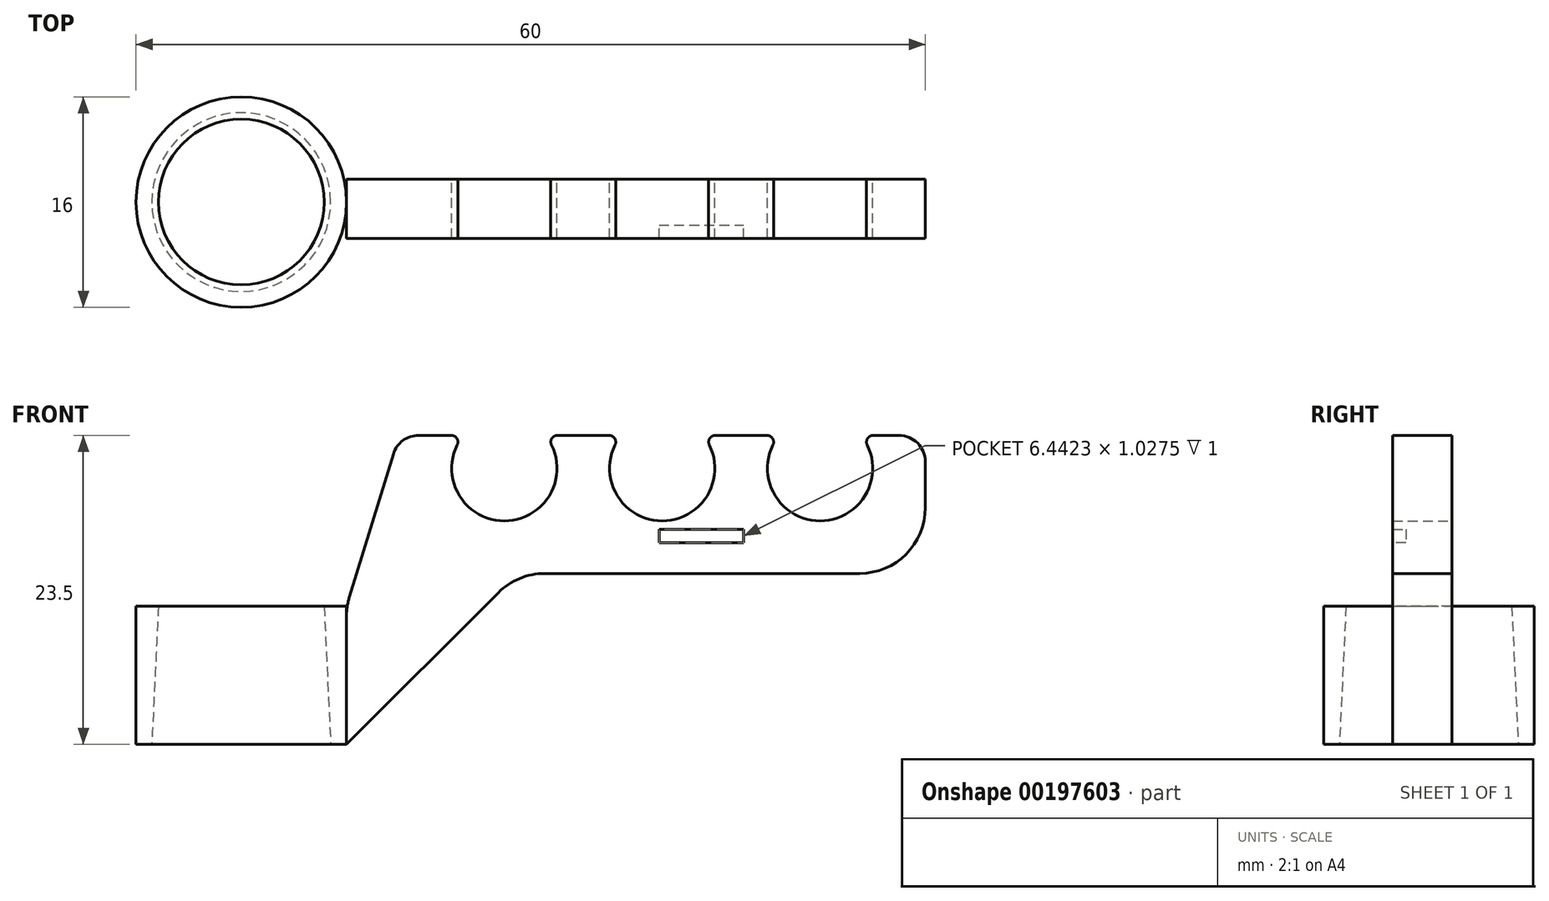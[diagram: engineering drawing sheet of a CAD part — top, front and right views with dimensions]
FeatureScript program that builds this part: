
annotation { "Feature Type Name" : "Feature", "Feature Type Description" : "" }
export const myFeature = defineFeature(function(context is Context, id is Id, definition is map)
    precondition{}
    {
        {
            var Q0;
            Q0=qCreatedBy(makeId("Top.planeOp"),FACE);
            var sketch = newSketch(context, id + "F0", { "sketchPlane" : qUnion([Q0])});
            skCircle(sketch, "E0", {"center": v(0, 0) * mm, "radius": 6.3 * mm});
            skCircle(sketch, "E1", {"center": v(0, 0) * mm, "radius": 8 * mm});
            skCircle(sketch, "E2", {"center": v(0, 0) * mm, "radius": 6.8 * mm});
            skSolve(sketch);
        }
        {
            var Q0;
            Q0=qCreatedBy(makeId("Front.planeOp"),FACE);
            var sketch = newSketch(context, id + "F1", { "sketchPlane" : qUnion([Q0])});
            skLineSegment(sketch, "E3.0", {"start": v(-6.8, 0) * mm, "end": v(6.8, 0) * mm});
            skLineSegment(sketch, "E4.0", {"start": v(-6.3, 0) * mm, "end": v(6.3, 0) * mm});
            skLineSegment(sketch, "E5.0", {"start": v(-8, 0) * mm, "end": v(-5.58, 0) * mm});
            skLineSegment(sketch, "E6", {"start": v(0, 0) * mm, "end": v(0, 10.5) * mm});
            skLineSegment(sketch, "E7.top", {"start": v(-8, 10.5) * mm, "end": v(-6.3, 10.5) * mm});
            skLineSegment(sketch, "E7.left", {"start": v(-8, 0) * mm, "end": v(-8, 10.5) * mm});
            skLineSegment(sketch, "E8", {"start": v(-6.3, 10.5) * mm, "end": v(-6.8, 0) * mm});
            skLineSegment(sketch, "E9.trimOffspring", {"start": v(0, 0) * mm, "end": v(8, 0) * mm});
            skSolve(sketch);
        }
        {
            var Q0;
            Q0=makeQuery(id+"F1.imprint","IMPRINT",FACE,{"disambiguationData":[TD([[makeQuery(id+"F1.imprint","IMPRINT",EDGE,{"derivedFrom":sQuery(id+"F1.wireOp",EDGE,"E7.top")}),-1.0]])]});
            var Q1;
            Q1=sQuery(id+"F1.wireOp",EDGE,"E6");
            revolve(context, id + "F2", {"entities" : qUnion([Q0]), "axis" : qUnion([Q1]), "revolveType" : RevolveType.FULL});
        }
        {
            var Q0;
            Q0=qCreatedBy(makeId("Front.planeOp"),FACE);
            var sketch = newSketch(context, id + "F3", { "sketchPlane" : qUnion([Q0])});
            skLineSegment(sketch, "E10", {"start": v(8, 10.5) * mm, "end": v(8, 0) * mm});
            skLineSegment(sketch, "E11.0", {"start": v(8, 10.5) * mm, "end": v(-8, 10.5) * mm});
            skLineSegment(sketch, "E12.0", {"start": v(-8, 0) * mm, "end": v(8, 0) * mm});
            skLineSegment(sketch, "E13", {"start": v(0, 13) * mm, "end": v(41.13, 13) * mm, "construction": true});
            skLineSegment(sketch, "E14", {"start": v(0, 21) * mm, "end": v(40.48, 21) * mm, "construction": true});
            skLineSegment(sketch, "E15", {"start": v(20, 25.73) * mm, "end": v(20, 4.34) * mm, "construction": true});
            skCircle(sketch, "E16", {"center": v(20, 21) * mm, "radius": 4 * mm});
            skCircle(sketch, "E17.1.0.0", {"center": v(32, 21) * mm, "radius": 4 * mm});
            skCircle(sketch, "E17.2.0.0", {"center": v(44, 21) * mm, "radius": 4 * mm});
            skLineSegment(sketch, "E17.direction1", {"start": v(20, 21) * mm, "end": v(32, 21) * mm, "construction": true});
            skLineSegment(sketch, "E18", {"start": v(12, 25.64) * mm, "end": v(12, 16.43) * mm, "construction": true});
            skLineSegment(sketch, "E19", {"start": v(12, 23.5) * mm, "end": v(68.02, 23.5) * mm});
            skLineSegment(sketch, "E20", {"start": v(52, 26.61) * mm, "end": v(52, 15.45) * mm, "construction": true});
            skLineSegment(sketch, "E21", {"start": v(12, 23.5) * mm, "end": v(8, 10.5) * mm});
            skLineSegment(sketch, "E22", {"start": v(22.25, 13) * mm, "end": v(41.13, 13) * mm});
            skLineSegment(sketch, "E23", {"start": v(52, 13) * mm, "end": v(52, 23.5) * mm});
            skLineSegment(sketch, "E24", {"start": v(8, 0) * mm, "end": v(21, 13) * mm});
            skPoint(sketch, "E25.orphan", {"position": v(22.25, 14.25) * mm});
            skLineSegment(sketch, "E26", {"start": v(21, 13) * mm, "end": v(22.25, 13) * mm});
            skLineSegment(sketch, "E27", {"start": v(41.13, 13) * mm, "end": v(52, 13) * mm});
            skLineSegment(sketch, "E28.bottom", {"start": v(8, 10.5) * mm, "end": v(7.8, 10.5) * mm});
            skLineSegment(sketch, "E28.top", {"start": v(8, 0) * mm, "end": v(7.8, 0) * mm});
            skLineSegment(sketch, "E28.right", {"start": v(7.8, 10.5) * mm, "end": v(7.8, 0) * mm});
            skSolve(sketch);
        }
        {
            var Q0;
            {var subQ0=sQuery(id+"F3.wireOp",EDGE,"E21");Q0=makeQuery(id+"F3.imprint","IMPRINT",FACE,{"disambiguationData":[TD([[makeQuery(id+"F3.imprint","IMPRINT",EDGE,{"derivedFrom":subQ0}),1.0]])]});}
            var Q1;
            Q1=makeQuery(id+"F3.imprint","IMPRINT",FACE,{"disambiguationData":[TD([[makeQuery(id+"F3.imprint","IMPRINT",EDGE,{"derivedFrom":sQuery(id+"F3.wireOp",EDGE,"E28.bottom")}),1.0]])]});
            extrude(context, id + "F4", {"entities" : qUnion([Q0, Q1]), "operationType" : NewBodyOperationType.ADD, "endBound" : BoundingType.SYMMETRIC, "depth" : 3.5 * mm});
        }
        {
            var Q0;
            Q0=makeQuery(id+"F4.boolean.opBoolean","INTERSECT",EDGE,{"derivedFrom":[makeQuery(id+"F2.opRevolve","SWEPT_FACE",FACE,{"disambiguationData":[OSD([sQuery(id+"F1.wireOp",EDGE,"E7.left")])]}),makeQuery(id+"F4.opExtrude","CAP_FACE",FACE,{"disambiguationData":[OSD([sQuery(id+"F3.wireOp",EDGE,"E16"),sQuery(id+"F3.wireOp",EDGE,"E17.1.0.0"),sQuery(id+"F3.wireOp",EDGE,"E17.2.0.0"),sQuery(id+"F3.wireOp",EDGE,"E17.3.0.0"),sQuery(id+"F3.wireOp",EDGE,"E19"),sQuery(id+"F3.wireOp",EDGE,"E21"),sQuery(id+"F3.wireOp",EDGE,"E22"),sQuery(id+"F3.wireOp",EDGE,"E23"),sQuery(id+"F3.wireOp",EDGE,"E24"),sQuery(id+"F3.wireOp",EDGE,"E26"),sQuery(id+"F3.wireOp",EDGE,"E27"),sQuery(id+"F3.wireOp",EDGE,"E28.bottom"),sQuery(id+"F3.wireOp",EDGE,"E28.top"),sQuery(id+"F3.wireOp",EDGE,"E28.right")])],"isStart":true})]});
            var Q1;
            Q1=makeQuery(id+"F4.boolean.opBoolean","INTERSECT",EDGE,{"derivedFrom":[makeQuery(id+"F2.opRevolve","SWEPT_FACE",FACE,{"disambiguationData":[OSD([sQuery(id+"F1.wireOp",EDGE,"E7.left")])]}),makeQuery(id+"F4.opExtrude","CAP_FACE",FACE,{"disambiguationData":[OSD([sQuery(id+"F3.wireOp",EDGE,"E16"),sQuery(id+"F3.wireOp",EDGE,"E17.1.0.0"),sQuery(id+"F3.wireOp",EDGE,"E17.2.0.0"),sQuery(id+"F3.wireOp",EDGE,"E17.3.0.0"),sQuery(id+"F3.wireOp",EDGE,"E19"),sQuery(id+"F3.wireOp",EDGE,"E21"),sQuery(id+"F3.wireOp",EDGE,"E22"),sQuery(id+"F3.wireOp",EDGE,"E23"),sQuery(id+"F3.wireOp",EDGE,"E24"),sQuery(id+"F3.wireOp",EDGE,"E26"),sQuery(id+"F3.wireOp",EDGE,"E27"),sQuery(id+"F3.wireOp",EDGE,"E28.bottom"),sQuery(id+"F3.wireOp",EDGE,"E28.top"),sQuery(id+"F3.wireOp",EDGE,"E28.right")])],"isStart":false})]});
            var Q2;
            Q2=makeQuery(id+"F4.opExtrude","SWEPT_EDGE",EDGE,{"disambiguationData":[OSD([sQuery(id+"F3.wireOp",EDGE,"E24"),sQuery(id+"F3.wireOp",EDGE,"E26")])]});
            var Q3;
            Q3=makeQuery(id+"F4.opExtrude","SWEPT_EDGE",EDGE,{"disambiguationData":[OSD([sQuery(id+"F3.wireOp",EDGE,"E23"),sQuery(id+"F3.wireOp",EDGE,"E27")])]});
            fillet(context, id + "F5", {"entities" : qUnion([Q0, Q1, Q2, Q3]), "radius" : 5 * mm, "tangentPropagation" : true, "allowEdgeOverflow" : false});
        }
        {
            var Q0;
            Q0=makeQuery(id+"F4.opExtrude","SWEPT_EDGE",EDGE,{"disambiguationData":[OSD([sQuery(id+"F3.wireOp",EDGE,"E19"),sQuery(id+"F3.wireOp",EDGE,"E21")])]});
            var Q1;
            Q1=makeQuery(id+"F4.opExtrude","SWEPT_EDGE",EDGE,{"disambiguationData":[OSD([sQuery(id+"F3.wireOp",EDGE,"E19"),sQuery(id+"F3.wireOp",EDGE,"E23")])]});
            fillet(context, id + "F6", {"entities" : qUnion([Q0, Q1]), "radius" : 2 * mm, "tangentPropagation" : true, "allowEdgeOverflow" : false});
        }
        {
            var Q0;
            {var subQ0=sQuery(id+"F3.wireOp",EDGE,"E19");var subQ1=sQuery(id+"F3.wireOp",EDGE,"E16");Q0=makeQuery(id+"F4.opExtrude","SWEPT_EDGE",EDGE,{"disambiguationData":[OSD([subQ1,subQ0]),TDD([makeQuery(id+"F3.imprint","INTERSECT",VERTEX,{"disambiguationData":[OD(1.0)],"derivedFrom":[subQ1,subQ0]})])]});}
            var Q1;
            {var subQ0=sQuery(id+"F3.wireOp",EDGE,"E19");var subQ1=sQuery(id+"F3.wireOp",EDGE,"E16");Q1=makeQuery(id+"F4.opExtrude","SWEPT_EDGE",EDGE,{"disambiguationData":[OSD([subQ1,subQ0]),TDD([makeQuery(id+"F3.imprint","INTERSECT",VERTEX,{"disambiguationData":[OD(0.0)],"derivedFrom":[subQ1,subQ0]})])]});}
            var Q2;
            {var subQ0=sQuery(id+"F3.wireOp",EDGE,"E19");var subQ1=sQuery(id+"F3.wireOp",EDGE,"E17.1.0.0");Q2=makeQuery(id+"F4.opExtrude","SWEPT_EDGE",EDGE,{"disambiguationData":[OSD([subQ1,subQ0]),TDD([makeQuery(id+"F3.imprint","INTERSECT",VERTEX,{"disambiguationData":[OD(0.0)],"derivedFrom":[subQ1,subQ0]})])]});}
            var Q3;
            {var subQ0=sQuery(id+"F3.wireOp",EDGE,"E19");var subQ1=sQuery(id+"F3.wireOp",EDGE,"E17.2.0.0");Q3=makeQuery(id+"F4.opExtrude","SWEPT_EDGE",EDGE,{"disambiguationData":[OSD([subQ1,subQ0]),TDD([makeQuery(id+"F3.imprint","INTERSECT",VERTEX,{"disambiguationData":[OD(0.0)],"derivedFrom":[subQ1,subQ0]})])]});}
            var Q4;
            {var subQ0=sQuery(id+"F3.wireOp",EDGE,"E19");var subQ1=sQuery(id+"F3.wireOp",EDGE,"E17.3.0.0");Q4=makeQuery(id+"F4.opExtrude","SWEPT_EDGE",EDGE,{"disambiguationData":[OSD([subQ1,subQ0]),TDD([makeQuery(id+"F3.imprint","INTERSECT",VERTEX,{"disambiguationData":[OD(0.0)],"derivedFrom":[subQ1,subQ0]})])]});}
            var Q5;
            {var subQ0=sQuery(id+"F3.wireOp",EDGE,"E19");var subQ1=sQuery(id+"F3.wireOp",EDGE,"E17.1.0.0");Q5=makeQuery(id+"F4.opExtrude","SWEPT_EDGE",EDGE,{"disambiguationData":[OSD([subQ1,subQ0]),TDD([makeQuery(id+"F3.imprint","INTERSECT",VERTEX,{"disambiguationData":[OD(1.0)],"derivedFrom":[subQ1,subQ0]})])]});}
            var Q6;
            {var subQ0=sQuery(id+"F3.wireOp",EDGE,"E19");var subQ1=sQuery(id+"F3.wireOp",EDGE,"E17.2.0.0");Q6=makeQuery(id+"F4.opExtrude","SWEPT_EDGE",EDGE,{"disambiguationData":[OSD([subQ1,subQ0]),TDD([makeQuery(id+"F3.imprint","INTERSECT",VERTEX,{"disambiguationData":[OD(1.0)],"derivedFrom":[subQ1,subQ0]})])]});}
            var Q7;
            {var subQ0=sQuery(id+"F3.wireOp",EDGE,"E19");var subQ1=sQuery(id+"F3.wireOp",EDGE,"E17.3.0.0");Q7=makeQuery(id+"F4.opExtrude","SWEPT_EDGE",EDGE,{"disambiguationData":[OSD([subQ1,subQ0]),TDD([makeQuery(id+"F3.imprint","INTERSECT",VERTEX,{"disambiguationData":[OD(1.0)],"derivedFrom":[subQ1,subQ0]})])]});}
            fillet(context, id + "F7", {"entities" : qUnion([Q0, Q1, Q2, Q3, Q4, Q5, Q6, Q7]), "radius" : .5 * mm, "tangentPropagation" : true, "allowEdgeOverflow" : false});
        }
        {
            var Q0;
            Q0=makeQuery(id+"F4.opExtrude","CAP_FACE",FACE,{"disambiguationData":[OSD([sQuery(id+"F3.wireOp",EDGE,"E16"),sQuery(id+"F3.wireOp",EDGE,"E17.1.0.0"),sQuery(id+"F3.wireOp",EDGE,"E17.2.0.0"),sQuery(id+"F3.wireOp",EDGE,"E17.3.0.0"),sQuery(id+"F3.wireOp",EDGE,"E19"),sQuery(id+"F3.wireOp",EDGE,"E21"),sQuery(id+"F3.wireOp",EDGE,"E22"),sQuery(id+"F3.wireOp",EDGE,"E23"),sQuery(id+"F3.wireOp",EDGE,"E24"),sQuery(id+"F3.wireOp",EDGE,"E26"),sQuery(id+"F3.wireOp",EDGE,"E27"),sQuery(id+"F3.wireOp",EDGE,"E28.bottom"),sQuery(id+"F3.wireOp",EDGE,"E28.top"),sQuery(id+"F3.wireOp",EDGE,"E28.right")])],"isStart":false});
            var sketch = newSketch(context, id + "F8", { "sketchPlane" : qUnion([Q0])});
            skFitSpline(sketch, "E29", {"points": [v(35.71, 16.35) * mm, v(35.78, 16.55) * mm, v(35.85, 16.65) * mm, v(35.98, 16.75) * mm, v(36.12, 16.8) * mm, v(36.24, 16.8) * mm, v(42.55, 16.82) * mm, v(42.65, 16.78) * mm, v(42.7, 16.65) * mm, v(42.65, 16.52) * mm, v(42.55, 16.36) * mm, v(42.42, 16.32) * mm, v(42.3, 16.26) * mm, v(42.08, 15.9) * mm, v(41.89, 15.83) * mm, v(41.78, 15.76) * mm, v(41.62, 15.48) * mm, v(41.45, 15.38) * mm, v(38.77, 14.57) * mm, v(38.7, 14.56) * mm, v(38.62, 14.38) * mm, v(38.56, 14.27) * mm, v(38.18, 14.06) * mm, v(38.06, 14.02) * mm, v(35.9, 13.44) * mm, v(35.75, 13.44) * mm, v(35.65, 13.48) * mm, v(35.59, 13.53) * mm, v(35, 14.06) * mm, v(34.97, 14.05) * mm, v(34.9, 14.03) * mm, v(34.85, 14) * mm, v(34.31, 13.47) * mm, v(34.24, 13.44) * mm, v(34.16, 13.44) * mm, v(31.77, 14.07) * mm, v(31.41, 14.28) * mm, v(31.3, 14.48) * mm, v(31.22, 14.57) * mm, v(31.12, 14.6) * mm, v(28.44, 15.4) * mm, v(28.33, 15.52) * mm, v(28.2, 15.88) * mm, v(28.14, 15.83) * mm, v(28.02, 15.85) * mm, v(27.94, 15.87) * mm, v(27.88, 15.92) * mm, v(27.69, 16.27) * mm, v(27.65, 16.3) * mm, v(27.51, 16.3) * mm, v(27.46, 16.32) * mm, v(27.28, 16.62) * mm, v(27.28, 16.7) * mm, v(27.33, 16.77) * mm, v(27.4, 16.8) * mm, v(27.46, 16.8) * mm, v(33.8, 16.81) * mm, v(33.85, 16.81) * mm, v(33.97, 16.77) * mm, v(34.17, 16.6) * mm, v(34.2, 16.5) * mm, v(34.25, 16.4) * mm, v(34.26, 16.34) * mm, v(34.33, 16.34) * mm, v(35.58, 16.34) * mm, v(35.71, 16.35) * mm]});
            skFitSpline(sketch, "E30", {"points": [v(30.68, 16.8) * mm, v(30.83, 16.69) * mm, v(30.9, 16.62) * mm, v(30.99, 16.5) * mm, v(31.06, 16.33) * mm, v(31.28, 16.02) * mm, v(31.53, 15.67) * mm, v(31.6, 15.6) * mm, v(32.13, 15.09) * mm, v(32.73, 14.67) * mm, v(33.36, 14.37) * mm, v(33.87, 14.2) * mm, v(34.55, 14.1) * mm, v(35, 14.06) * mm, v(35.61, 14.1) * mm, v(36.24, 14.24) * mm, v(36.81, 14.44) * mm, v(37.3, 14.7) * mm, v(37.8, 15.05) * mm, v(38.1, 15.33) * mm, v(38.48, 15.75) * mm, v(38.72, 16.05) * mm, v(38.93, 16.39) * mm, v(39.08, 16.63) * mm, v(39.22, 16.76) * mm, v(39.4, 16.82) * mm, v(39.46, 16.82) * mm], "startDerivative": vector(6.61, -4.14) * mm, "endDerivative": vector(2.94, -0.27) * mm});
            skLineSegment(sketch, "E31.bottom", {"start": v(31.76, 16.35) * mm, "end": v(38.2, 16.35) * mm});
            skLineSegment(sketch, "E31.top", {"start": v(31.76, 15.33) * mm, "end": v(38.2, 15.33) * mm});
            skLineSegment(sketch, "E31.left", {"start": v(31.76, 16.35) * mm, "end": v(31.76, 15.33) * mm});
            skLineSegment(sketch, "E31.right", {"start": v(38.2, 16.35) * mm, "end": v(38.2, 15.33) * mm});
            skLineSegment(sketch, "E32", {"start": v(27.69, 16.27) * mm, "end": v(31.76, 16.35) * mm});
            skLineSegment(sketch, "E33", {"start": v(31.76, 16.1) * mm, "end": v(28.2, 15.88) * mm});
            skLineSegment(sketch, "E34", {"start": v(31.76, 15.88) * mm, "end": v(28.44, 15.4) * mm});
            skLineSegment(sketch, "E35", {"start": v(31.76, 15.67) * mm, "end": v(29.25, 15.15) * mm});
            skLineSegment(sketch, "E36", {"start": v(31.76, 15.33) * mm, "end": v(30.28, 14.84) * mm});
            skLineSegment(sketch, "E37", {"start": v(32.82, 15.33) * mm, "end": v(31.22, 14.57) * mm});
            skLineSegment(sketch, "E38", {"start": v(33.59, 15.33) * mm, "end": v(31.77, 14.07) * mm});
            skLineSegment(sketch, "E39", {"start": v(34.05, 15.33) * mm, "end": v(32.59, 13.83) * mm});
            skLineSegment(sketch, "E40", {"start": v(34.4, 15.33) * mm, "end": v(33.39, 13.61) * mm});
            skLineSegment(sketch, "E41", {"start": v(34.73, 15.33) * mm, "end": v(34.16, 13.44) * mm});
            skLineSegment(sketch, "E42", {"start": v(34.98, 15.33) * mm, "end": v(34.97, 14.05) * mm});
            skLineSegment(sketch, "E43", {"start": v(35.26, 15.33) * mm, "end": v(35.81, 13.43) * mm});
            skLineSegment(sketch, "E44", {"start": v(35.61, 15.33) * mm, "end": v(36.58, 13.6) * mm});
            skLineSegment(sketch, "E45", {"start": v(35.96, 15.33) * mm, "end": v(37.37, 13.83) * mm});
            skLineSegment(sketch, "E46", {"start": v(36.38, 15.33) * mm, "end": v(38.18, 14.06) * mm});
            skLineSegment(sketch, "E47", {"start": v(37.14, 15.33) * mm, "end": v(38.77, 14.57) * mm});
            skLineSegment(sketch, "E48", {"start": v(38.2, 15.33) * mm, "end": v(39.77, 14.85) * mm});
            skLineSegment(sketch, "E49", {"start": v(38.2, 15.65) * mm, "end": v(40.68, 15.13) * mm});
            skLineSegment(sketch, "E50", {"start": v(38.2, 15.87) * mm, "end": v(41.57, 15.43) * mm});
            skLineSegment(sketch, "E51", {"start": v(38.2, 16.1) * mm, "end": v(42.02, 15.86) * mm});
            skLineSegment(sketch, "E52", {"start": v(38.2, 16.3) * mm, "end": v(42.35, 16.3) * mm});
            skSolve(sketch);
        }
        {
            var Q0;
            {var subQ0=sQuery(id+"F8.wireOp",EDGE,"E36");Q0=makeQuery(id+"F8.imprint","IMPRINT",FACE,{"disambiguationData":[TD([[makeQuery(id+"F8.imprint","IMPRINT",EDGE,{"derivedFrom":subQ0}),-1.0]])]});}
            var Q1;
            {var subQ0=sQuery(id+"F8.wireOp",EDGE,"E46");var subQ1=sQuery(id+"F8.wireOp",EDGE,"E29");var subQ2=makeQuery(id+"F8.imprint","INTERSECT",VERTEX,{"derivedFrom":[subQ1,subQ0]});Q1=makeQuery(id+"F8.imprint","IMPRINT",FACE,{"disambiguationData":[TD([[makeQuery(id+"F8.imprint","IMPRINT",EDGE,{"disambiguationData":[TD([[subQ2,1.0]])],"derivedFrom":subQ1}),-1.0]])]});}
            var Q2;
            {var subQ0=sQuery(id+"F8.wireOp",EDGE,"E38");var subQ1=sQuery(id+"F8.wireOp",EDGE,"E29");var subQ2=makeQuery(id+"F8.imprint","INTERSECT",VERTEX,{"derivedFrom":[subQ1,subQ0]});Q2=makeQuery(id+"F8.imprint","IMPRINT",FACE,{"disambiguationData":[TD([[makeQuery(id+"F8.imprint","IMPRINT",EDGE,{"disambiguationData":[TD([[subQ2,1.0]])],"derivedFrom":subQ1}),-1.0]])]});}
            var Q3;
            {var subQ0=sQuery(id+"F8.wireOp",EDGE,"E44");var subQ1=sQuery(id+"F8.wireOp",EDGE,"E30");var subQ2=makeQuery(id+"F8.imprint","INTERSECT",VERTEX,{"derivedFrom":[subQ1,subQ0]});Q3=makeQuery(id+"F8.imprint","IMPRINT",FACE,{"disambiguationData":[TD([[makeQuery(id+"F8.imprint","IMPRINT",EDGE,{"disambiguationData":[TD([[subQ2,-1.0]])],"derivedFrom":subQ1}),1.0]])]});}
            var Q4;
            {var subQ0=sQuery(id+"F8.wireOp",EDGE,"E39");var subQ1=sQuery(id+"F8.wireOp",EDGE,"E29");var subQ2=makeQuery(id+"F8.imprint","INTERSECT",VERTEX,{"derivedFrom":[subQ1,subQ0]});Q4=makeQuery(id+"F8.imprint","IMPRINT",FACE,{"disambiguationData":[TD([[makeQuery(id+"F8.imprint","IMPRINT",EDGE,{"disambiguationData":[TD([[subQ2,1.0]])],"derivedFrom":subQ1}),-1.0]])]});}
            var Q5;
            {var subQ0=sQuery(id+"F8.wireOp",EDGE,"E43");var subQ1=sQuery(id+"F8.wireOp",EDGE,"E30");var subQ2=makeQuery(id+"F8.imprint","INTERSECT",VERTEX,{"derivedFrom":[subQ1,subQ0]});Q5=makeQuery(id+"F8.imprint","IMPRINT",FACE,{"disambiguationData":[TD([[makeQuery(id+"F8.imprint","IMPRINT",EDGE,{"disambiguationData":[TD([[subQ2,-1.0]])],"derivedFrom":subQ1}),1.0]])]});}
            var Q6;
            {var subQ0=sQuery(id+"F8.wireOp",EDGE,"E30");var subQ1=sQuery(id+"F8.wireOp",EDGE,"E29");var subQ2=makeQuery(id+"F8.imprint","INTERSECT",VERTEX,{"disambiguationData":[OD(0.0)],"derivedFrom":[subQ1,subQ0]});Q6=makeQuery(id+"F8.imprint","IMPRINT",FACE,{"disambiguationData":[TD([[makeQuery(id+"F8.imprint","IMPRINT",EDGE,{"disambiguationData":[TD([[subQ2,-1.0]])],"derivedFrom":subQ1}),-1.0]])]});}
            var Q7;
            {var subQ0=sQuery(id+"F8.wireOp",EDGE,"E41");var subQ1=sQuery(id+"F8.wireOp",EDGE,"E30");var subQ2=makeQuery(id+"F8.imprint","INTERSECT",VERTEX,{"derivedFrom":[subQ1,subQ0]});Q7=makeQuery(id+"F8.imprint","IMPRINT",FACE,{"disambiguationData":[TD([[makeQuery(id+"F8.imprint","IMPRINT",EDGE,{"disambiguationData":[TD([[subQ2,-1.0]])],"derivedFrom":subQ1}),1.0]])]});}
            var Q8;
            {var subQ0=sQuery(id+"F8.wireOp",EDGE,"E32");var subQ1=sQuery(id+"F8.wireOp",EDGE,"E30");var subQ2=makeQuery(id+"F8.imprint","INTERSECT",VERTEX,{"derivedFrom":[subQ1,subQ0]});Q8=makeQuery(id+"F8.imprint","IMPRINT",FACE,{"disambiguationData":[TD([[makeQuery(id+"F8.imprint","IMPRINT",EDGE,{"disambiguationData":[TD([[subQ2,-1.0]])],"derivedFrom":subQ1}),1.0]])]});}
            var Q9;
            {var subQ0=sQuery(id+"F8.wireOp",EDGE,"E48");Q9=makeQuery(id+"F8.imprint","IMPRINT",FACE,{"disambiguationData":[TD([[makeQuery(id+"F8.imprint","IMPRINT",EDGE,{"derivedFrom":subQ0}),-1.0]])]});}
            var Q10;
            {var subQ0=sQuery(id+"F8.wireOp",EDGE,"E32");var subQ1=sQuery(id+"F8.wireOp",EDGE,"E29");var subQ2=makeQuery(id+"F8.imprint","INTERSECT",VERTEX,{"derivedFrom":[subQ1,subQ0]});Q10=makeQuery(id+"F8.imprint","IMPRINT",FACE,{"disambiguationData":[TD([[makeQuery(id+"F8.imprint","IMPRINT",EDGE,{"disambiguationData":[TD([[subQ2,1.0]])],"derivedFrom":subQ1}),-1.0]])]});}
            var Q11;
            {var subQ0=sQuery(id+"F8.wireOp",EDGE,"E40");var subQ1=sQuery(id+"F8.wireOp",EDGE,"E30");var subQ2=makeQuery(id+"F8.imprint","INTERSECT",VERTEX,{"derivedFrom":[subQ1,subQ0]});Q11=makeQuery(id+"F8.imprint","IMPRINT",FACE,{"disambiguationData":[TD([[makeQuery(id+"F8.imprint","IMPRINT",EDGE,{"disambiguationData":[TD([[subQ2,-1.0]])],"derivedFrom":subQ1}),1.0]])]});}
            var Q12;
            {var subQ3=sQuery(id+"F8.wireOp",EDGE,"E29");var subQ7=sQuery(id+"F8.wireOp",EDGE,"E30");var subQ8=makeQuery(id+"F8.imprint","INTERSECT",VERTEX,{"disambiguationData":[OD(2.0)],"derivedFrom":[subQ3,subQ7]});Q12=makeQuery(id+"F8.imprint","IMPRINT",FACE,{"disambiguationData":[TD([[makeQuery(id+"F8.imprint","IMPRINT",EDGE,{"disambiguationData":[TD([[subQ8,1.0]])],"derivedFrom":subQ3}),-1.0]])]});}
            var Q13;
            {var subQ0=sQuery(id+"F8.wireOp",EDGE,"E48");Q13=makeQuery(id+"F8.imprint","IMPRINT",FACE,{"disambiguationData":[TD([[makeQuery(id+"F8.imprint","IMPRINT",EDGE,{"derivedFrom":subQ0}),1.0]])]});}
            var Q14;
            {var subQ0=sQuery(id+"F8.wireOp",EDGE,"E33");var subQ1=sQuery(id+"F8.wireOp",EDGE,"E29");var subQ2=makeQuery(id+"F8.imprint","INTERSECT",VERTEX,{"derivedFrom":[subQ1,subQ0]});Q14=makeQuery(id+"F8.imprint","IMPRINT",FACE,{"disambiguationData":[TD([[makeQuery(id+"F8.imprint","IMPRINT",EDGE,{"disambiguationData":[TD([[subQ2,1.0]])],"derivedFrom":subQ1}),-1.0]])]});}
            var Q15;
            {var subQ0=sQuery(id+"F8.wireOp",EDGE,"E39");var subQ1=sQuery(id+"F8.wireOp",EDGE,"E30");var subQ2=makeQuery(id+"F8.imprint","INTERSECT",VERTEX,{"derivedFrom":[subQ1,subQ0]});Q15=makeQuery(id+"F8.imprint","IMPRINT",FACE,{"disambiguationData":[TD([[makeQuery(id+"F8.imprint","IMPRINT",EDGE,{"disambiguationData":[TD([[subQ2,-1.0]])],"derivedFrom":subQ1}),1.0]])]});}
            var Q16;
            {var subQ0=sQuery(id+"F8.wireOp",EDGE,"E34");var subQ1=sQuery(id+"F8.wireOp",EDGE,"E29");var subQ2=makeQuery(id+"F8.imprint","INTERSECT",VERTEX,{"derivedFrom":[subQ1,subQ0]});Q16=makeQuery(id+"F8.imprint","IMPRINT",FACE,{"disambiguationData":[TD([[makeQuery(id+"F8.imprint","IMPRINT",EDGE,{"disambiguationData":[TD([[subQ2,1.0]])],"derivedFrom":subQ1}),-1.0]])]});}
            var Q17;
            {var subQ0=sQuery(id+"F8.wireOp",EDGE,"E46");var subQ1=sQuery(id+"F8.wireOp",EDGE,"E30");var subQ2=makeQuery(id+"F8.imprint","INTERSECT",VERTEX,{"derivedFrom":[subQ1,subQ0]});Q17=makeQuery(id+"F8.imprint","IMPRINT",FACE,{"disambiguationData":[TD([[makeQuery(id+"F8.imprint","IMPRINT",EDGE,{"disambiguationData":[TD([[subQ2,-1.0]])],"derivedFrom":subQ1}),1.0]])]});}
            var Q18;
            {var subQ0=sQuery(id+"F8.wireOp",EDGE,"E38");var subQ1=sQuery(id+"F8.wireOp",EDGE,"E30");var subQ2=makeQuery(id+"F8.imprint","INTERSECT",VERTEX,{"derivedFrom":[subQ1,subQ0]});Q18=makeQuery(id+"F8.imprint","IMPRINT",FACE,{"disambiguationData":[TD([[makeQuery(id+"F8.imprint","IMPRINT",EDGE,{"disambiguationData":[TD([[subQ2,-1.0]])],"derivedFrom":subQ1}),1.0]])]});}
            var Q19;
            {var subQ0=sQuery(id+"F8.wireOp",EDGE,"E36");Q19=makeQuery(id+"F8.imprint","IMPRINT",FACE,{"disambiguationData":[TD([[makeQuery(id+"F8.imprint","IMPRINT",EDGE,{"derivedFrom":subQ0}),1.0]])]});}
            var Q20;
            {var subQ0=sQuery(id+"F8.wireOp",EDGE,"E44");var subQ1=sQuery(id+"F8.wireOp",EDGE,"E29");var subQ2=makeQuery(id+"F8.imprint","INTERSECT",VERTEX,{"derivedFrom":[subQ1,subQ0]});Q20=makeQuery(id+"F8.imprint","IMPRINT",FACE,{"disambiguationData":[TD([[makeQuery(id+"F8.imprint","IMPRINT",EDGE,{"disambiguationData":[TD([[subQ2,1.0]])],"derivedFrom":subQ1}),-1.0]])]});}
            var Q21;
            {var subQ0=sQuery(id+"F8.wireOp",EDGE,"E37");var subQ1=sQuery(id+"F8.wireOp",EDGE,"E30");var subQ2=makeQuery(id+"F8.imprint","INTERSECT",VERTEX,{"derivedFrom":[subQ1,subQ0]});Q21=makeQuery(id+"F8.imprint","IMPRINT",FACE,{"disambiguationData":[TD([[makeQuery(id+"F8.imprint","IMPRINT",EDGE,{"disambiguationData":[TD([[subQ2,-1.0]])],"derivedFrom":subQ1}),1.0]])]});}
            var Q22;
            {var subQ5=sQuery(id+"F8.wireOp",EDGE,"E30");var subQ6=sQuery(id+"F8.wireOp",EDGE,"E29");var subQ9=makeQuery(id+"F8.imprint","INTERSECT",VERTEX,{"disambiguationData":[OD(3.0)],"derivedFrom":[subQ6,subQ5]});Q22=makeQuery(id+"F8.imprint","IMPRINT",FACE,{"disambiguationData":[TD([[makeQuery(id+"F8.imprint","IMPRINT",EDGE,{"disambiguationData":[TD([[subQ9,-1.0]])],"derivedFrom":subQ6}),-1.0]])]});}
            var Q23;
            {var subQ0=sQuery(id+"F8.wireOp",EDGE,"E45");var subQ1=sQuery(id+"F8.wireOp",EDGE,"E29");var subQ2=makeQuery(id+"F8.imprint","INTERSECT",VERTEX,{"derivedFrom":[subQ1,subQ0]});Q23=makeQuery(id+"F8.imprint","IMPRINT",FACE,{"disambiguationData":[TD([[makeQuery(id+"F8.imprint","IMPRINT",EDGE,{"disambiguationData":[TD([[subQ2,1.0]])],"derivedFrom":subQ1}),-1.0]])]});}
            var Q24;
            {var subQ0=sQuery(id+"F8.wireOp",EDGE,"E30");var subQ1=sQuery(id+"F8.wireOp",EDGE,"E29");var subQ2=makeQuery(id+"F8.imprint","INTERSECT",VERTEX,{"disambiguationData":[OD(1.0)],"derivedFrom":[subQ1,subQ0]});Q24=makeQuery(id+"F8.imprint","IMPRINT",FACE,{"disambiguationData":[TD([[makeQuery(id+"F8.imprint","IMPRINT",EDGE,{"disambiguationData":[TD([[subQ2,1.0]])],"derivedFrom":subQ1}),-1.0]])]});}
            var Q25;
            {var subQ0=sQuery(id+"F8.wireOp",EDGE,"E47");var subQ1=sQuery(id+"F8.wireOp",EDGE,"E30");var subQ2=makeQuery(id+"F8.imprint","INTERSECT",VERTEX,{"derivedFrom":[subQ1,subQ0]});Q25=makeQuery(id+"F8.imprint","IMPRINT",FACE,{"disambiguationData":[TD([[makeQuery(id+"F8.imprint","IMPRINT",EDGE,{"disambiguationData":[TD([[subQ2,-1.0]])],"derivedFrom":subQ1}),1.0]])]});}
            var Q26;
            {var subQ0=sQuery(id+"F8.wireOp",EDGE,"E37");var subQ1=sQuery(id+"F8.wireOp",EDGE,"E29");var subQ2=makeQuery(id+"F8.imprint","INTERSECT",VERTEX,{"derivedFrom":[subQ1,subQ0]});Q26=makeQuery(id+"F8.imprint","IMPRINT",FACE,{"disambiguationData":[TD([[makeQuery(id+"F8.imprint","IMPRINT",EDGE,{"disambiguationData":[TD([[subQ2,1.0]])],"derivedFrom":subQ1}),-1.0]])]});}
            var Q27;
            {var subQ0=sQuery(id+"F8.wireOp",EDGE,"E45");var subQ1=sQuery(id+"F8.wireOp",EDGE,"E30");var subQ2=makeQuery(id+"F8.imprint","INTERSECT",VERTEX,{"derivedFrom":[subQ1,subQ0]});Q27=makeQuery(id+"F8.imprint","IMPRINT",FACE,{"disambiguationData":[TD([[makeQuery(id+"F8.imprint","IMPRINT",EDGE,{"disambiguationData":[TD([[subQ2,-1.0]])],"derivedFrom":subQ1}),1.0]])]});}
            var Q28;
            {var subQ0=sQuery(id+"F8.wireOp",EDGE,"E30");var subQ1=sQuery(id+"F8.wireOp",EDGE,"E29");var subQ2=makeQuery(id+"F8.imprint","INTERSECT",VERTEX,{"disambiguationData":[OD(0.0)],"derivedFrom":[subQ1,subQ0]});Q28=makeQuery(id+"F8.imprint","IMPRINT",FACE,{"disambiguationData":[TD([[makeQuery(id+"F8.imprint","IMPRINT",EDGE,{"disambiguationData":[TD([[subQ2,1.0]])],"derivedFrom":subQ1}),-1.0]])]});}
            var Q29;
            {var subQ0=sQuery(id+"F8.wireOp",EDGE,"E31.bottom");var subQ1=sQuery(id+"F8.wireOp",EDGE,"E29");var subQ2=makeQuery(id+"F8.imprint","INTERSECT",VERTEX,{"disambiguationData":[OD(0.0)],"derivedFrom":[subQ1,subQ0]});Q29=makeQuery(id+"F8.imprint","IMPRINT",FACE,{"disambiguationData":[TD([[makeQuery(id+"F8.imprint","IMPRINT",EDGE,{"disambiguationData":[TD([[subQ2,-1.0]])],"derivedFrom":subQ1}),1.0]])]});}
            var Q30;
            {var subQ0=sQuery(id+"F8.wireOp",EDGE,"E50");var subQ1=sQuery(id+"F8.wireOp",EDGE,"E29");var subQ2=makeQuery(id+"F8.imprint","INTERSECT",VERTEX,{"derivedFrom":[subQ1,subQ0]});Q30=makeQuery(id+"F8.imprint","IMPRINT",FACE,{"disambiguationData":[TD([[makeQuery(id+"F8.imprint","IMPRINT",EDGE,{"disambiguationData":[TD([[subQ2,1.0]])],"derivedFrom":subQ1}),-1.0]])]});}
            var Q31;
            {var subQ0=sQuery(id+"F8.wireOp",EDGE,"E51");var subQ1=sQuery(id+"F8.wireOp",EDGE,"E29");var subQ2=makeQuery(id+"F8.imprint","INTERSECT",VERTEX,{"derivedFrom":[subQ1,subQ0]});Q31=makeQuery(id+"F8.imprint","IMPRINT",FACE,{"disambiguationData":[TD([[makeQuery(id+"F8.imprint","IMPRINT",EDGE,{"disambiguationData":[TD([[subQ2,1.0]])],"derivedFrom":subQ1}),-1.0]])]});}
            var Q32;
            {var subQ0=sQuery(id+"F8.wireOp",EDGE,"E49");var subQ1=sQuery(id+"F8.wireOp",EDGE,"E29");var subQ2=makeQuery(id+"F8.imprint","INTERSECT",VERTEX,{"derivedFrom":[subQ1,subQ0]});Q32=makeQuery(id+"F8.imprint","IMPRINT",FACE,{"disambiguationData":[TD([[makeQuery(id+"F8.imprint","IMPRINT",EDGE,{"disambiguationData":[TD([[subQ2,1.0]])],"derivedFrom":subQ1}),-1.0]])]});}
            var Q33;
            {var subQ0=sQuery(id+"F8.wireOp",EDGE,"E51");var subQ1=sQuery(id+"F8.wireOp",EDGE,"E30");var subQ2=makeQuery(id+"F8.imprint","INTERSECT",VERTEX,{"derivedFrom":[subQ1,subQ0]});Q33=makeQuery(id+"F8.imprint","IMPRINT",FACE,{"disambiguationData":[TD([[makeQuery(id+"F8.imprint","IMPRINT",EDGE,{"disambiguationData":[TD([[subQ2,-1.0]])],"derivedFrom":subQ1}),1.0]])]});}
            var Q34;
            {var subQ0=sQuery(id+"F8.wireOp",EDGE,"E50");var subQ1=sQuery(id+"F8.wireOp",EDGE,"E30");var subQ2=makeQuery(id+"F8.imprint","INTERSECT",VERTEX,{"derivedFrom":[subQ1,subQ0]});Q34=makeQuery(id+"F8.imprint","IMPRINT",FACE,{"disambiguationData":[TD([[makeQuery(id+"F8.imprint","IMPRINT",EDGE,{"disambiguationData":[TD([[subQ2,-1.0]])],"derivedFrom":subQ1}),1.0]])]});}
            var Q35;
            {var subQ0=sQuery(id+"F8.wireOp",EDGE,"E49");var subQ1=sQuery(id+"F8.wireOp",EDGE,"E30");var subQ2=makeQuery(id+"F8.imprint","INTERSECT",VERTEX,{"derivedFrom":[subQ1,subQ0]});Q35=makeQuery(id+"F8.imprint","IMPRINT",FACE,{"disambiguationData":[TD([[makeQuery(id+"F8.imprint","IMPRINT",EDGE,{"disambiguationData":[TD([[subQ2,-1.0]])],"derivedFrom":subQ1}),1.0]])]});}
            var Q36;
            {var subQ0=sQuery(id+"F8.wireOp",EDGE,"E33");var subQ1=sQuery(id+"F8.wireOp",EDGE,"E30");var subQ2=makeQuery(id+"F8.imprint","INTERSECT",VERTEX,{"derivedFrom":[subQ1,subQ0]});Q36=makeQuery(id+"F8.imprint","IMPRINT",FACE,{"disambiguationData":[TD([[makeQuery(id+"F8.imprint","IMPRINT",EDGE,{"disambiguationData":[TD([[subQ2,-1.0]])],"derivedFrom":subQ1}),1.0]])]});}
            var Q37;
            {var subQ0=sQuery(id+"F8.wireOp",EDGE,"E31.top");var subQ1=sQuery(id+"F8.wireOp",EDGE,"E30");var subQ2=makeQuery(id+"F8.imprint","INTERSECT",VERTEX,{"disambiguationData":[OD(0.0)],"derivedFrom":[subQ1,subQ0]});Q37=makeQuery(id+"F8.imprint","IMPRINT",FACE,{"disambiguationData":[TD([[makeQuery(id+"F8.imprint","IMPRINT",EDGE,{"disambiguationData":[TD([[subQ2,-1.0]])],"derivedFrom":subQ1}),1.0]])]});}
            var Q38;
            {var subQ0=sQuery(id+"F8.wireOp",EDGE,"E34");var subQ1=sQuery(id+"F8.wireOp",EDGE,"E30");var subQ2=makeQuery(id+"F8.imprint","INTERSECT",VERTEX,{"derivedFrom":[subQ1,subQ0]});Q38=makeQuery(id+"F8.imprint","IMPRINT",FACE,{"disambiguationData":[TD([[makeQuery(id+"F8.imprint","IMPRINT",EDGE,{"disambiguationData":[TD([[subQ2,-1.0]])],"derivedFrom":subQ1}),1.0]])]});}
            var Q39;
            {var subQ0=sQuery(id+"F8.wireOp",EDGE,"E31.right");var subQ1=sQuery(id+"F8.wireOp",EDGE,"E30");var subQ2=makeQuery(id+"F8.imprint","INTERSECT",VERTEX,{"derivedFrom":[subQ1,subQ0]});Q39=makeQuery(id+"F8.imprint","IMPRINT",FACE,{"disambiguationData":[TD([[makeQuery(id+"F8.imprint","IMPRINT",EDGE,{"disambiguationData":[TD([[subQ2,-1.0]])],"derivedFrom":subQ1}),1.0]])]});}
            var Q40;
            {var subQ0=sQuery(id+"F8.wireOp",EDGE,"E35");var subQ1=sQuery(id+"F8.wireOp",EDGE,"E30");var subQ2=makeQuery(id+"F8.imprint","INTERSECT",VERTEX,{"derivedFrom":[subQ1,subQ0]});Q40=makeQuery(id+"F8.imprint","IMPRINT",FACE,{"disambiguationData":[TD([[makeQuery(id+"F8.imprint","IMPRINT",EDGE,{"disambiguationData":[TD([[subQ2,-1.0]])],"derivedFrom":subQ1}),1.0]])]});}
            var Q41;
            {var subQ0=sQuery(id+"F8.wireOp",EDGE,"E30");var subQ1=sQuery(id+"F8.wireOp",EDGE,"E29");var subQ2=makeQuery(id+"F8.imprint","INTERSECT",VERTEX,{"disambiguationData":[OD(1.0)],"derivedFrom":[subQ1,subQ0]});Q41=makeQuery(id+"F8.imprint","IMPRINT",FACE,{"disambiguationData":[TD([[makeQuery(id+"F8.imprint","IMPRINT",EDGE,{"disambiguationData":[TD([[subQ2,1.0]])],"derivedFrom":subQ1}),1.0]])]});}
            var Q42;
            {var subQ0=sQuery(id+"F8.wireOp",EDGE,"E31.top");var subQ1=sQuery(id+"F8.wireOp",EDGE,"E30");var subQ2=makeQuery(id+"F8.imprint","INTERSECT",VERTEX,{"disambiguationData":[OD(1.0)],"derivedFrom":[subQ1,subQ0]});Q42=makeQuery(id+"F8.imprint","IMPRINT",FACE,{"disambiguationData":[TD([[makeQuery(id+"F8.imprint","IMPRINT",EDGE,{"disambiguationData":[TD([[subQ2,-1.0]])],"derivedFrom":subQ1}),-1.0]])]});}
            var Q43;
            {var subQ0=sQuery(id+"F8.wireOp",EDGE,"E31.left");var subQ1=sQuery(id+"F8.wireOp",EDGE,"E30");var subQ2=makeQuery(id+"F8.imprint","INTERSECT",VERTEX,{"derivedFrom":[subQ1,subQ0]});Q43=makeQuery(id+"F8.imprint","IMPRINT",FACE,{"disambiguationData":[TD([[makeQuery(id+"F8.imprint","IMPRINT",EDGE,{"disambiguationData":[TD([[subQ2,-1.0]])],"derivedFrom":subQ1}),-1.0]])]});}
            var Q44;
            {var subQ0=sQuery(id+"F8.wireOp",EDGE,"E30");var subQ1=sQuery(id+"F8.wireOp",EDGE,"E29");var subQ2=makeQuery(id+"F8.imprint","INTERSECT",VERTEX,{"disambiguationData":[OD(3.0)],"derivedFrom":[subQ1,subQ0]});Q44=makeQuery(id+"F8.imprint","IMPRINT",FACE,{"disambiguationData":[TD([[makeQuery(id+"F8.imprint","IMPRINT",EDGE,{"disambiguationData":[TD([[subQ2,-1.0]])],"derivedFrom":subQ1}),1.0]])]});}
            var Q45;
            {var subQ0=sQuery(id+"F8.wireOp",EDGE,"E42");var subQ1=sQuery(id+"F8.wireOp",EDGE,"E29");var subQ2=makeQuery(id+"F8.imprint","INTERSECT",VERTEX,{"derivedFrom":[subQ1,subQ0]});Q45=makeQuery(id+"F8.imprint","IMPRINT",FACE,{"disambiguationData":[TD([[makeQuery(id+"F8.imprint","IMPRINT",EDGE,{"disambiguationData":[TD([[subQ2,1.0]])],"derivedFrom":subQ1}),-1.0]])]});}
            var Q46;
            {var subQ0=sQuery(id+"F8.wireOp",EDGE,"E40");var subQ1=sQuery(id+"F8.wireOp",EDGE,"E29");var subQ2=makeQuery(id+"F8.imprint","INTERSECT",VERTEX,{"derivedFrom":[subQ1,subQ0]});Q46=makeQuery(id+"F8.imprint","IMPRINT",FACE,{"disambiguationData":[TD([[makeQuery(id+"F8.imprint","IMPRINT",EDGE,{"disambiguationData":[TD([[subQ2,1.0]])],"derivedFrom":subQ1}),-1.0]])]});}
            var Q47;
            {var subQ0=sQuery(id+"F8.wireOp",EDGE,"E41");var subQ1=sQuery(id+"F8.wireOp",EDGE,"E29");var subQ2=makeQuery(id+"F8.imprint","INTERSECT",VERTEX,{"derivedFrom":[subQ1,subQ0]});Q47=makeQuery(id+"F8.imprint","IMPRINT",FACE,{"disambiguationData":[TD([[makeQuery(id+"F8.imprint","IMPRINT",EDGE,{"disambiguationData":[TD([[subQ2,1.0]])],"derivedFrom":subQ1}),-1.0]])]});}
            var Q48;
            {var subQ0=sQuery(id+"F8.wireOp",EDGE,"E43");var subQ1=sQuery(id+"F8.wireOp",EDGE,"E29");var subQ2=makeQuery(id+"F8.imprint","INTERSECT",VERTEX,{"derivedFrom":[subQ1,subQ0]});Q48=makeQuery(id+"F8.imprint","IMPRINT",FACE,{"disambiguationData":[TD([[makeQuery(id+"F8.imprint","IMPRINT",EDGE,{"disambiguationData":[TD([[subQ2,-1.0]])],"derivedFrom":subQ1}),-1.0]])]});}
            var Q49;
            {var subQ0=sQuery(id+"F8.wireOp",EDGE,"E43");var subQ1=sQuery(id+"F8.wireOp",EDGE,"E29");var subQ2=makeQuery(id+"F8.imprint","INTERSECT",VERTEX,{"derivedFrom":[subQ1,subQ0]});Q49=makeQuery(id+"F8.imprint","IMPRINT",FACE,{"disambiguationData":[TD([[makeQuery(id+"F8.imprint","IMPRINT",EDGE,{"disambiguationData":[TD([[subQ2,1.0]])],"derivedFrom":subQ1}),-1.0]])]});}
            var Q50;
            {var subQ1=sQuery(id+"F8.wireOp",EDGE,"E31.bottom");var subQ20=sQuery(id+"F8.wireOp",EDGE,"E29");var subQ24=makeQuery(id+"F8.imprint","INTERSECT",VERTEX,{"disambiguationData":[OD(0.0)],"derivedFrom":[subQ20,subQ1]});Q50=makeQuery(id+"F8.imprint","IMPRINT",FACE,{"disambiguationData":[TD([[makeQuery(id+"F8.imprint","IMPRINT",EDGE,{"disambiguationData":[TD([[subQ24,-1.0]])],"derivedFrom":subQ20}),-1.0]])]});}
            extrude(context, id + "F9", {"entities" : qUnion([Q0, Q1, Q2, Q3, Q4, Q5, Q6, Q7, Q8, Q9, Q10, Q11, Q12, Q13, Q14, Q15, Q16, Q17, Q18, Q19, Q20, Q21, Q22, Q23, Q24, Q25, Q26, Q27, Q28, Q29, Q30, Q31, Q32, Q33, Q34, Q35, Q36, Q37, Q38, Q39, Q40, Q41, Q42, Q43, Q44, Q45, Q46, Q47, Q48, Q49, Q50]), "operationType" : NewBodyOperationType.ADD, "depth" : 1 * mm});
        }
        {
            var Q0;
            Q0=makeQuery(id+"F9.opExtrude","CAP_FACE",FACE,{"disambiguationData":[OSD([sQuery(id+"F8.wireOp",EDGE,"E29"),sQuery(id+"F8.wireOp",EDGE,"E30"),sQuery(id+"F8.wireOp",EDGE,"E31.bottom")])],"isStart":false});
            var sketch = newSketch(context, id + "F10", { "sketchPlane" : qUnion([Q0])});
            skLineSegment(sketch, "E53.0", {"start": v(31.76, 16.35) * mm, "end": v(38.2, 16.35) * mm});
            skLineSegment(sketch, "E54.0", {"start": v(31.76, 16.35) * mm, "end": v(31.76, 15.33) * mm});
            skLineSegment(sketch, "E55.0", {"start": v(31.76, 15.33) * mm, "end": v(38.2, 15.33) * mm});
            skLineSegment(sketch, "E56.0", {"start": v(38.2, 16.35) * mm, "end": v(38.2, 15.33) * mm});
            skLineSegment(sketch, "E57", {"start": v(31.76, 16.25) * mm, "end": v(38.2, 16.25) * mm});
            skSolve(sketch);
        }
        {
            var Q0;
            {var subQ0=sQuery(id+"F10.wireOp",EDGE,"E55.0");Q0=makeQuery(id+"F10.imprint","IMPRINT",FACE,{"disambiguationData":[TD([[makeQuery(id+"F10.imprint","IMPRINT",EDGE,{"derivedFrom":subQ0}),1.0]])]});}
            extrude(context, id + "F11", {"entities" : qUnion([Q0]), "operationType" : NewBodyOperationType.REMOVE, "oppositeDirection" : true, "depth" : 1 * mm});
        }
        {
            var Q0;
            Q0=makeQuery(id+"F4.opExtrude","SWEPT_EDGE",EDGE,{"disambiguationData":[OSD([sQuery(id+"F3.wireOp",EDGE,"E21"),sQuery(id+"F3.wireOp",EDGE,"E28.bottom"),sQuery(id+"F3.wireOp",EDGE,"E10")])]});
            fillet(context, id + "F12", {"entities" : qUnion([Q0]), "radius" : 5 * mm, "tangentPropagation" : true, "allowEdgeOverflow" : false});
        }
    });
